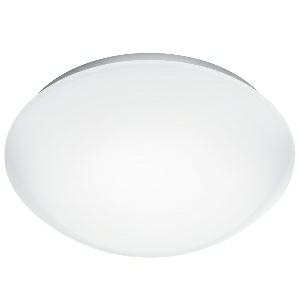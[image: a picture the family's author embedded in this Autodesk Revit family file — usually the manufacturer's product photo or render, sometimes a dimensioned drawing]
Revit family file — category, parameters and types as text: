
# Revit family: rs_pro_led_p3_sl_056131
name_source: partatom
category: Leuchten
revit_build: Autodesk Revit 2016 (Build: 20190508_0715(x64)
units: mm (PartAtom-declared; Revit-internal decimal feet)

## family parameters
Basisbauteil = Fläche
Beim Laden mit Abzugskörper schneiden = Nein
Bemaßung runder Anschluss = Durchmesser verwenden
Gemeinsam genutzt = Nein
Lichtquelle = Nein
Raumberechnungspunkt = Nein
Teiletyp = Normal

## types (1)
- RS PRO LED P3 SL (1 x , 2210 lm, 3000 K)
    Beschreibung = Dimensions (Ø x H): 400 x 142 mm; Mains power supply: 220 – 240 V / 50 – 60 Hz; Output: 19,5 W; Luminous flux: 2210 lm; Colour temperature: 3000 K; Colour variation LED: SDCM3; Colour Rendering Index CRI: 80-89; With lamp: Yes, STEINEL LED system; Lamp: LED cannot be replaced; LED life expectancy (max. °C): 50000 h; Drop in luminous flux in accordance with LM80: L80B10; Base: without; LED cooling system: Passive Thermo Control; With motion detector: No; Photo-cell controller: No; Basic light level function: No; Soft light start: Yes; Impact resistance: IK03; IP-rating: IP54; Protection class: II; Ambient temperature: 10 – 40 °C; Housing material: Plastic; Cover material: Plastic, opal; Manufacturer's Warranty: 5 years; With remote control: No; Version: warm white; PU1, EAN: 4007841056131
    CIE Flux Codes = 39 67 87 85 100
    Color Rendering = 80-89
    Color Temperature = 3000 K
    Frequency = 60 Hz, 50 Hz
    Height = 0 mm  [stored 0 ft]
    Hersteller = Steinel
    Lamp Light Flux = 2210 lm
    Lamp count = 1
    Lampe = 1 x
    Length = 400 mm
    Luminous efficacy = 116 lm/W
    ModVariant = Nein
    Modell = 056131
    Mounting Type = Surface mounted
    Number of Poles = 1
    OnlyDefault = Ja
    Power Factor = 1
    Product Name = RS PRO LED P3 SL
    Product group = Sensor-switched indoor light
    ProductGroupID = 30
    Protection Class = Protection class II
    Protection Degree = IP 54
    RlxData = <blob elided: 37397 chars, md5=08adaead>
    Scheinlast = 19 VA
    Socket = socket
    Standby Power = 0 W
    System Light Flux = 2210 lm
    System Power = 19 W
    Typenbild = produkt1_056131.jpg
    Typenkommentare = Product without accessories
    URL = http://relux.com
    VarID = ---
    Voltage = 0 V
    Vorgabe-Ansicht = 1800 mm
    Weight = 0.00 kg
    Width = 0 mm  [stored 0 ft]

note: [stored X ft] marks values corroborated as IEEE doubles in the binary element streams (Revit-internal decimal feet)

## geometry (parser evidence)
native form markers: Sweep x16
no freeform markers — native parametric forms only
